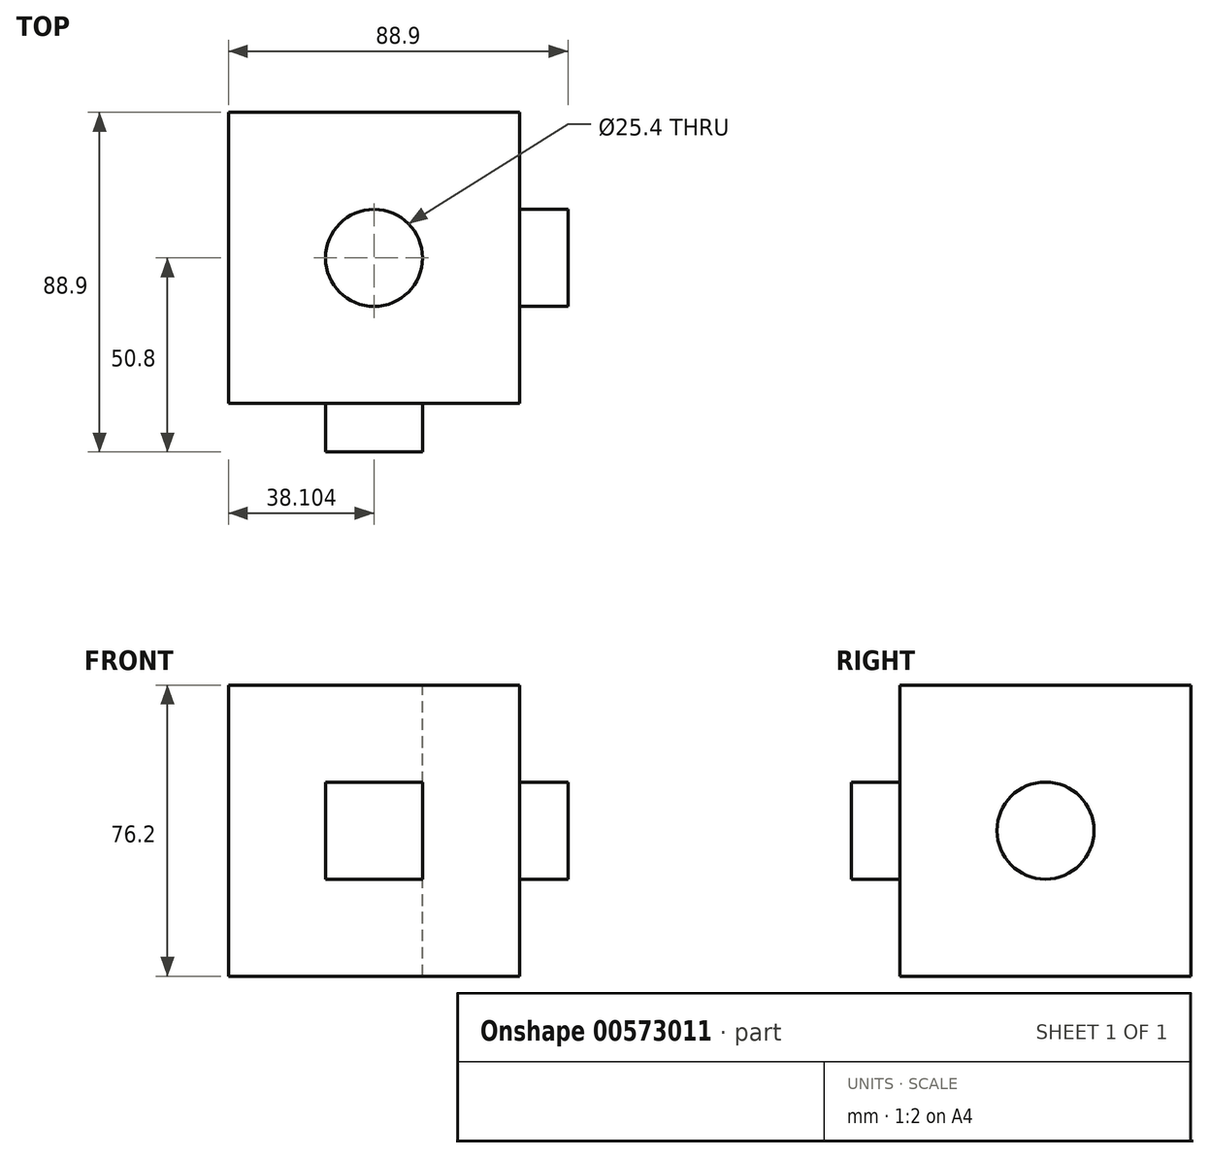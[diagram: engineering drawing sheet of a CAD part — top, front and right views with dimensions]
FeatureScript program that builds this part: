
annotation { "Feature Type Name" : "Feature", "Feature Type Description" : "" }
export const myFeature = defineFeature(function(context is Context, id is Id, definition is map)
    precondition{}
    {
        {
            var Q0;
            Q0=qCreatedBy(makeId("Front.planeOp"),FACE);
            var sketch = newSketch(context, id + "F0", { "sketchPlane" : qUnion([Q0])});
            skLineSegment(sketch, "E0.bottom", {"start": v(-37.44, -33.34) * mm, "end": v(38.76, -33.34) * mm});
            skLineSegment(sketch, "E0.top", {"start": v(-37.44, 42.86) * mm, "end": v(38.76, 42.86) * mm});
            skLineSegment(sketch, "E0.left", {"start": v(-37.44, -33.34) * mm, "end": v(-37.44, 42.86) * mm});
            skLineSegment(sketch, "E0.right", {"start": v(38.76, -33.34) * mm, "end": v(38.76, 42.86) * mm});
            skSolve(sketch);
        }
        {
            var Q0;
            Q0=makeQuery(id+"F0.imprint","IMPRINT",FACE,{"disambiguationData":[TD([[makeQuery(id+"F0.imprint","IMPRINT",EDGE,{"derivedFrom":sQuery(id+"F0.wireOp",EDGE,"E0.bottom")}),1.0]])]});
            extrude(context, id + "F1", {"entities" : qUnion([Q0]), "depth" : 76.2 * mm, "offsetDistance" : 25.4 * mm});
        }
        {
            var Q0;
            Q0=makeQuery(id+"F1.opExtrude","CAP_FACE",FACE,{"disambiguationData":[OSD([sQuery(id+"F0.wireOp",EDGE,"E0.bottom"),sQuery(id+"F0.wireOp",EDGE,"E0.top"),sQuery(id+"F0.wireOp",EDGE,"E0.left"),sQuery(id+"F0.wireOp",EDGE,"E0.right")])],"isStart":false});
            var sketch = newSketch(context, id + "F2", { "sketchPlane" : qUnion([Q0])});
            skLineSegment(sketch, "E1.bottom", {"start": v(-12.04, -7.94) * mm, "end": v(13.36, -7.94) * mm});
            skLineSegment(sketch, "E1.top", {"start": v(-12.04, 17.46) * mm, "end": v(13.36, 17.46) * mm});
            skLineSegment(sketch, "E1.left", {"start": v(-12.04, -7.94) * mm, "end": v(-12.04, 17.46) * mm});
            skLineSegment(sketch, "E1.right", {"start": v(13.36, -7.94) * mm, "end": v(13.36, 17.46) * mm});
            skSolve(sketch);
        }
        {
            var Q0;
            Q0=makeQuery(id+"F2.imprint","IMPRINT",FACE,{"disambiguationData":[TD([[makeQuery(id+"F2.imprint","IMPRINT",EDGE,{"derivedFrom":sQuery(id+"F2.wireOp",EDGE,"E1.bottom")}),1.0]])]});
            extrude(context, id + "F3", {"entities" : qUnion([Q0]), "operationType" : NewBodyOperationType.ADD, "depth" : 12.7 * mm, "offsetDistance" : 25.4 * mm});
        }
        {
            var Q0;
            Q0=makeQuery(id+"F1.opExtrude","SWEPT_FACE",FACE,{"disambiguationData":[OSD([sQuery(id+"F0.wireOp",EDGE,"E0.right")])]});
            var sketch = newSketch(context, id + "F4", { "sketchPlane" : qUnion([Q0])});
            skCircle(sketch, "E2", {"center": v(-38.1, 4.76) * mm, "radius": 12.7 * mm});
            skSolve(sketch);
        }
        {
            var Q0;
            Q0=makeQuery(id+"F4.imprint","IMPRINT",FACE,{"disambiguationData":[TD([[makeQuery(id+"F4.imprint","IMPRINT",EDGE,{"derivedFrom":sQuery(id+"F4.wireOp",EDGE,"E2")}),1.0]])]});
            extrude(context, id + "F5", {"entities" : qUnion([Q0]), "operationType" : NewBodyOperationType.ADD, "depth" : 12.7 * mm, "offsetDistance" : 25.4 * mm});
        }
        {
            var Q0;
            Q0=makeQuery(id+"F1.opExtrude","SWEPT_FACE",FACE,{"disambiguationData":[OSD([sQuery(id+"F0.wireOp",EDGE,"E0.top")])]});
            var sketch = newSketch(context, id + "F6", { "sketchPlane" : qUnion([Q0])});
            skPoint(sketch, "E3", {"position": v(0.66, -38.1) * mm});
            skSolve(sketch);
        }
        {
            var Q0;
            Q0=sQuery(id+"F6.wireOp",VERTEX,"E3");
            var Q1;
            Q1=makeQuery(id+"F1.opExtrude","SWEPT_BODY",BODY,{"disambiguationData":[OSD([sQuery(id+"F0.wireOp",EDGE,"E0.bottom"),sQuery(id+"F0.wireOp",EDGE,"E0.top"),sQuery(id+"F0.wireOp",EDGE,"E0.left"),sQuery(id+"F0.wireOp",EDGE,"E0.right")])]});
            hole(context, id + "F7", {"style" : HoleStyle.SIMPLE, "endStyle" : HoleEndStyle.THROUGH, "holeDiameter" : 25.4 * mm, "isTappedThrough" : true, "tappedDepth" : 12.7 * mm, "tapClearance" : 3, "locations" : qUnion([Q0]), "scope" : qUnion([Q1])});
        }
    });
